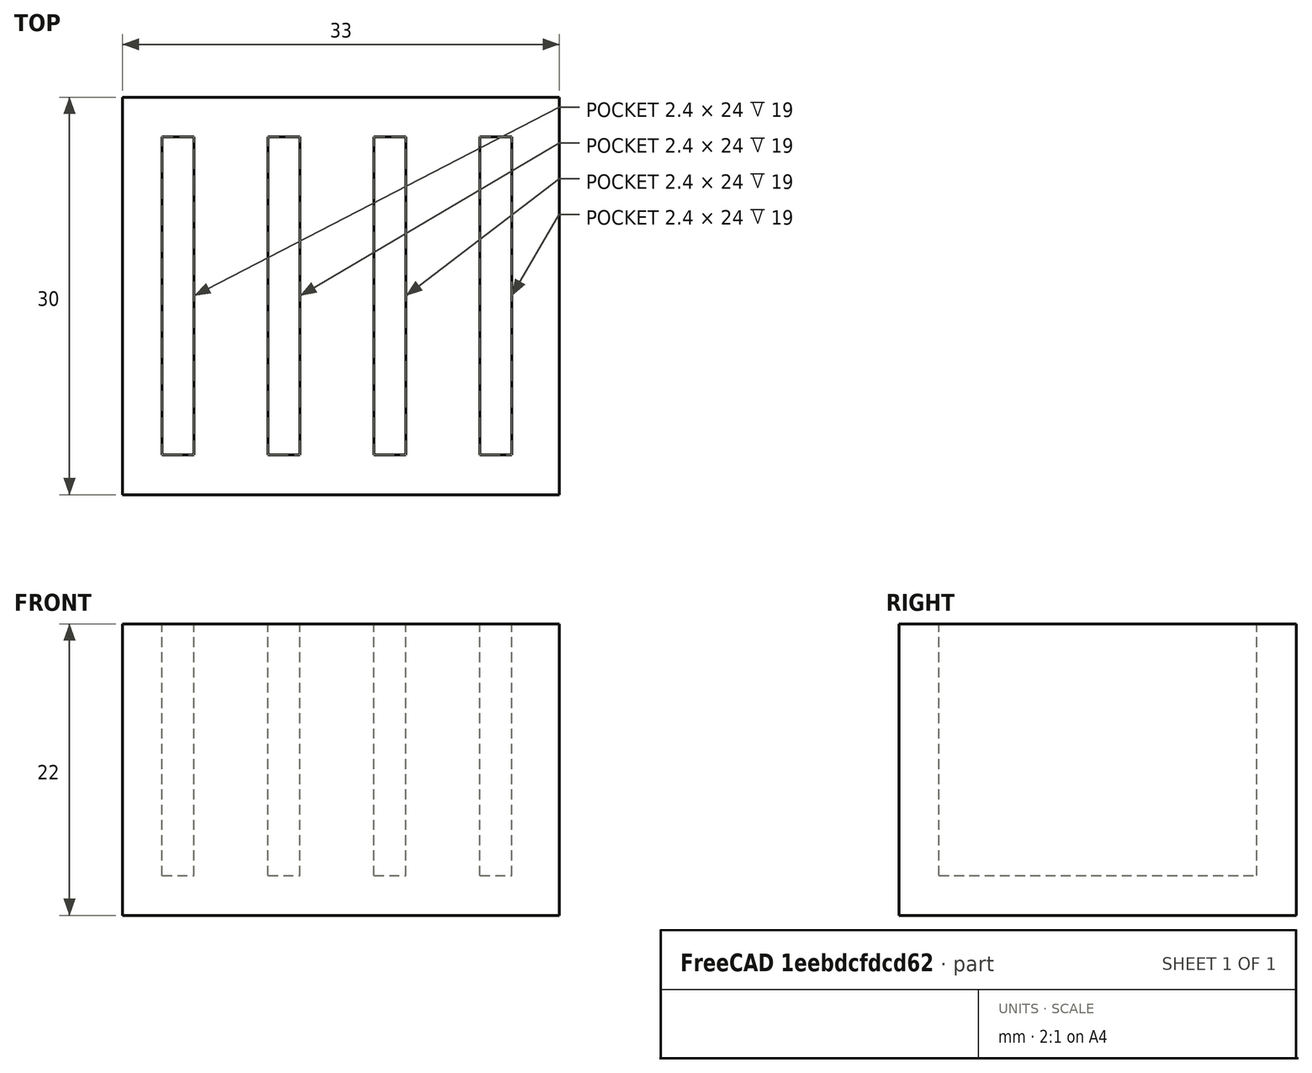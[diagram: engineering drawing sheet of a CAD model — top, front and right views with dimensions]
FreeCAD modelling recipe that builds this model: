
FCSTD DOCUMENT  (FreeCAD 0.21R33694 (Git))
Label: OJT1_T08R01_portasds
License: All rights reserved
LicenseURL: https://en.wikipedia.org/wiki/All_rights_reserved
objects: Part::Box×5, Part::MultiFuse×1, Part::Cut×1
note: 7 computed .brp shape members not serialized (recipe doc carries the construction recipe); baked Part::Feature solids carry a one-line shape summary decoded from their .brp

FEATURE [Part::Box] Box  label="Ranura_1"
  AttacherType = Attacher::AttachEngine3D
  Height = 22
  Length = 2.4
  Width = 24
FEATURE [Part::Box] Box001  label="Ranura_2"
  AttacherType = Attacher::AttachEngine3D
  Height = 22
  Length = 2.4
  Placement = pos=(8,0,0) rot=(0,0,1;0rad)
  Width = 24
FEATURE [Part::Box] Box002  label="Ranura_3"
  AttacherType = Attacher::AttachEngine3D
  Height = 22
  Length = 2.4
  Placement = pos=(16,0,0) rot=(0,0,1;0rad)
  Width = 24
FEATURE [Part::Box] Box003  label="Ranura_4"
  AttacherType = Attacher::AttachEngine3D
  Height = 22
  Length = 2.4
  Placement = pos=(24,0,0) rot=(0,0,1;0rad)
  Width = 24
FEATURE [Part::MultiFuse] Fusion  label="Ranuras"
  Placement = pos=(0,0,3) rot=(0,0,1;0rad)
  Shapes = -> [Box,Box001,Box002,Box003]
FEATURE [Part::Box] Box004  label="Base"
  AttacherType = Attacher::AttachEngine3D
  Height = 22
  Length = 33
  Placement = pos=(-3,-3,0) rot=(0,0,1;0rad)
  Width = 30
FEATURE [Part::Cut] Cut  label="Porta-sds"
  Base = -> Box004
  Tool = -> Fusion
